# Revit family: 0040012 Feilo Sylvania Lighting Fixture SYLBAY 4K TB L6VH AISLE DAL
name_source: partatom
category: Lighting Fixtures
revit_build: Autodesk Revit 2017 (Build: 20190507_1515(x64)
units: mm (PartAtom-declared; Revit-internal decimal feet)

## family parameters
Cut with Voids When Loaded = No
Host = Face
Light Source = No
OmniClass Number = 23.80.70.00
OmniClass Title = Lighting
Part Type = Normal
Room Calculation Point = No
Round Connector Dimension = Use Diameter
Shared = No

## types (1)
- 0040012 SYLBAY 4K TB L6VH AISLE DAL
    Apparent Load = 222 VA
    Assembly Code = D5020200
    AssetType = Fixed
    ClassificationName = Uniclass2015
    ClassificationValue = EF_70_80
    Cost = 0 $
    Default Elevation = 1219 mm
    Description = Logistics and Industry modular high bay luminaire with aisle optics to provide necessary illumination for narrow areas. Twin body with 6 optical modules, 34,285 lumens,  222W, 154lm/W, 4000K, CRI 80, aisle beam optic, DALI dimmable, 3 step MacAdam ellipse, grey finish (RAL7012), Class 1, 220-240V,IP65, IK08, (LxWxH) 726x386x133mm.
    DimmingControlOptions = Dimmable
    DocumentationLiterature = http://www.sylvania-lighting.com
    DurationUnit = hours
    ElectricShockClassification = Class I
    ExpectedLife = 50000
    Height = 133 mm
    IfcExportAs = IfcLightFixtureType
    IfcExportType = IfcLightFixtureType
    ImpactProtectionIndex = IK08
    IngressProtection = IP65
    InputNominalFrequency = 50/60 Hz
    InputVoltage = 220-240V~
    Keynote = 16500
    Lamp = LED
    LampColourRenderingIndex = 80
    LampColourTemperature = 4000 K
    LampMacAdamStep = 3
    LampNominalLuminous = 34285 lm
    LampsType = LED
    Length = 726 mm  [stored 2.38189 ft]
    LightOutputRatio = 100
    LuminousEfficacy = 154 lm/W
    Manufacturer = Feilo Sylvania
    ManufacturerName = Feilo Sylvania
    Material = aluminium housing, polycarbonate diffuser
    Material_1_FEILO = <By Category>
    Material_2_FEILO = <By Category>
    Material_3_FEILO = <By Category>
    Material_4_FEILO = <By Category>
    Model = SYLBAY 4K TB L6VH AISLE DAL
    ModelNumber = 0040012
    ModelReference = SYLBAY 4K TB L6VH AISLE DAL
    Name = SYLBAY 4K TB L6VH AISLE DAL
    NominalDepth = 386 mm  [stored 1.2664 ft]
    NominalHeight = 133 mm
    NominalLength = 410 mm
    PowerConsumption = 222 W
    PowerFactor = 0.98
    Type Image = <None>
    TypeName = SYLBAY 4K TB L6VH AISLE DAL
    URL = http://www.sylvania-lighting.com
    Voltage = 230 V
    Weight = 9.2 kg
    Width = 386 mm  [stored 1.2664 ft]

note: [stored X ft] marks values corroborated as IEEE doubles in the binary element streams (Revit-internal decimal feet)

## geometry (parser evidence)
native form markers: Sweep x5
no freeform markers — native parametric forms only
